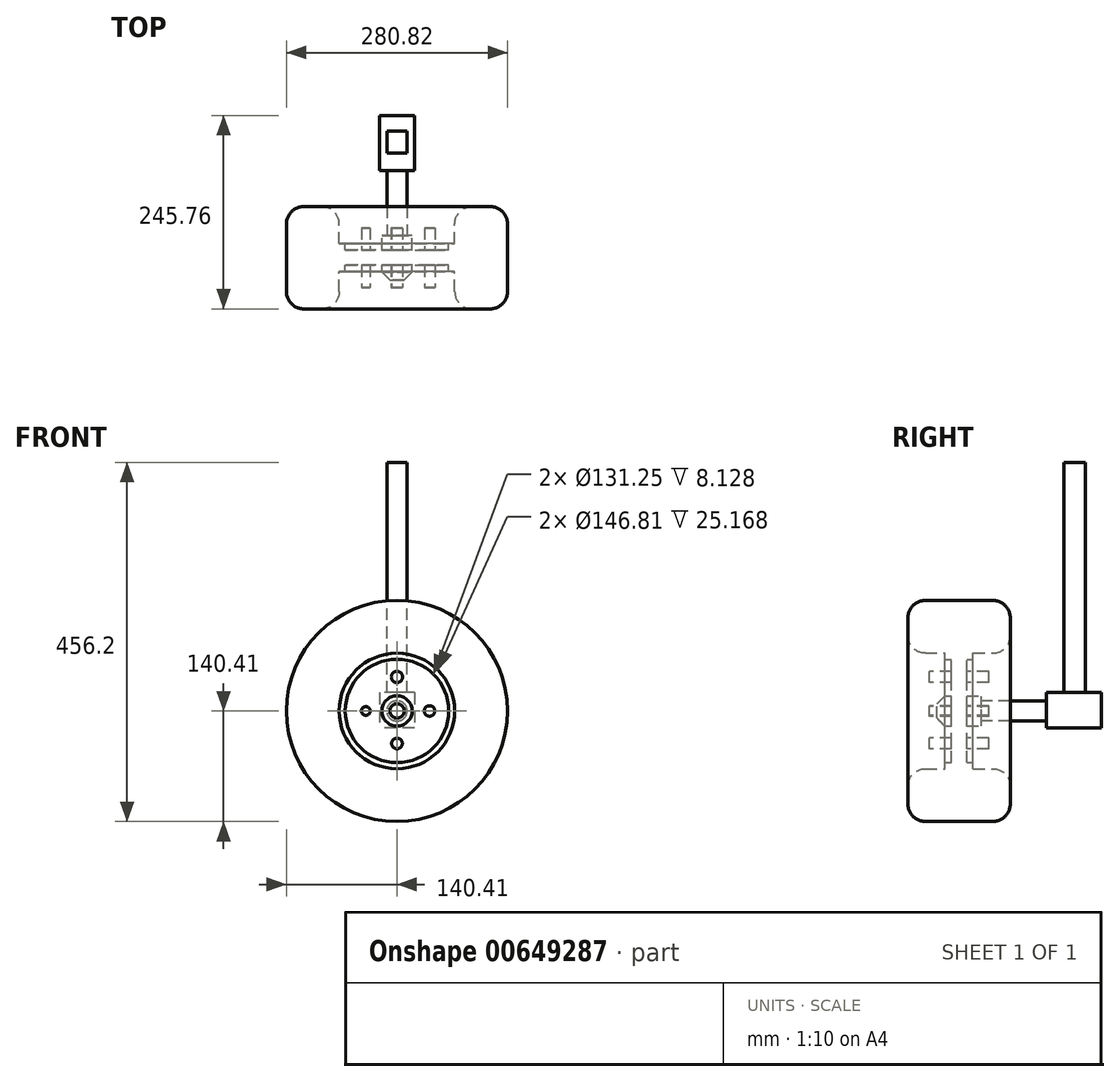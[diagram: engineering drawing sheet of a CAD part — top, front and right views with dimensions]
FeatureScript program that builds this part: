
annotation { "Feature Type Name" : "Feature", "Feature Type Description" : "" }
export const myFeature = defineFeature(function(context is Context, id is Id, definition is map)
    precondition{}
    {
        {
            var Q0;
            Q0=qCreatedBy(makeId("Front.planeOp"),FACE);
            var sketch = newSketch(context, id + "F0", { "sketchPlane" : qUnion([Q0])});
            skCircle(sketch, "E0", {"center": v(0, 0) * mm, "radius": 19.27 * mm});
            skSolve(sketch);
        }
        {
            var Q0;
            Q0 = qSketchRegion(id + "F0", true);
            extrude(context, id + "F1", {"entities" : qUnion([Q0]), "endBound" : BoundingType.SYMMETRIC, "depth" : 56.4 * mm, "offsetDistance" : 25.4 * mm});
        }
        {
            var Q0;
            Q0=qCreatedBy(makeId("Front.planeOp"),FACE);
            var sketch = newSketch(context, id + "F2", { "sketchPlane" : qUnion([Q0])});
            skCircle(sketch, "E1", {"center": v(0, 0) * mm, "radius": 76.72 * mm});
            skSolve(sketch);
        }
        {
            var Q0;
            Q0 = qSketchRegion(id + "F2", true);
            extrude(context, id + "F3", {"entities" : qUnion([Q0]), "operationType" : NewBodyOperationType.ADD, "endBound" : BoundingType.SYMMETRIC, "oppositeDirection" : true, "depth" : 19.3 * mm, "offsetDistance" : 25.4 * mm});
        }
        {
            var Q0;
            Q0=makeQuery(id+"F1.opExtrude","CAP_EDGE",EDGE,{"disambiguationData":[OSD([sQuery(id+"F0.wireOp",EDGE,"E0")])],"isStart":false});
            chamfer(context, id + "F4", {"entities" : qUnion([Q0]), "width" : 10.16 * mm, "tangentPropagation" : true});
        }
        {
            var Q0;
            Q0=qCreatedBy(makeId("Front.planeOp"),FACE);
            var sketch = newSketch(context, id + "F5", { "sketchPlane" : qUnion([Q0])});
            skCircle(sketch, "E2", {"center": v(0, 0) * mm, "radius": 65.62 * mm});
            skCircle(sketch, "E3", {"center": v(0, 0) * mm, "radius": 76.62 * mm});
            skSolve(sketch);
        }
        {
            var Q0;
            Q0 = qSketchRegion(id + "F5", true);
            extrude(context, id + "F6", {"entities" : qUnion([Q0]), "operationType" : NewBodyOperationType.ADD, "endBound" : BoundingType.SYMMETRIC, "depth" : 35.56 * mm, "offsetDistance" : 25.4 * mm});
        }
        {
            var Q0;
            Q0=qCreatedBy(makeId("Front.planeOp"),FACE);
            var sketch = newSketch(context, id + "F7", { "sketchPlane" : qUnion([Q0])});
            skCircle(sketch, "E4", {"center": v(0, 0) * mm, "radius": 140.41 * mm});
            skCircle(sketch, "E5", {"center": v(0, 0) * mm, "radius": 73.4 * mm});
            skSolve(sketch);
        }
        {
            var Q0;
            Q0 = qSketchRegion(id + "F7", true);
            extrude(context, id + "F8", {"entities" : qUnion([Q0]), "operationType" : NewBodyOperationType.ADD, "endBound" : BoundingType.SYMMETRIC, "depth" : 130.05 * mm, "offsetDistance" : 25.4 * mm});
        }
        {
            var Q0;
            Q0=makeQuery(id+"F8.opExtrude","CAP_EDGE",EDGE,{"disambiguationData":[OSD([sQuery(id+"F7.wireOp",EDGE,"E4")])],"isStart":true});
            var Q1;
            Q1=makeQuery(id+"F8.opExtrude","CAP_EDGE",EDGE,{"disambiguationData":[OSD([sQuery(id+"F7.wireOp",EDGE,"E5")])],"isStart":true});
            var Q2;
            Q2=makeQuery(id+"F8.opExtrude","CAP_EDGE",EDGE,{"disambiguationData":[OSD([sQuery(id+"F7.wireOp",EDGE,"E4")])],"isStart":false});
            var Q3;
            Q3=makeQuery(id+"F8.opExtrude","CAP_EDGE",EDGE,{"disambiguationData":[OSD([sQuery(id+"F7.wireOp",EDGE,"E5")])],"isStart":false});
            fillet(context, id + "F9", {"entities" : qUnion([Q0, Q1, Q2, Q3]), "radius" : 22.08 * mm, "tangentPropagation" : true, "allowEdgeOverflow" : false});
        }
        {
            var Q0;
            Q0=qCreatedBy(makeId("Front.planeOp"),FACE);
            var sketch = newSketch(context, id + "F10", { "sketchPlane" : qUnion([Q0])});
            skCircle(sketch, "E6", {"center": v(0, 43.2) * mm, "radius": 7.25 * mm});
            skCircle(sketch, "E7", {"center": v(41.43, 0) * mm, "radius": 6.66 * mm});
            skCircle(sketch, "E8", {"center": v(0, -41.27) * mm, "radius": 6.8 * mm});
            skCircle(sketch, "E9", {"center": v(-39.5, 0) * mm, "radius": 5.52 * mm});
            skSolve(sketch);
        }
        {
            var Q0;
            Q0 = qSketchRegion(id + "F10", true);
            extrude(context, id + "F11", {"entities" : qUnion([Q0]), "operationType" : NewBodyOperationType.ADD, "endBound" : BoundingType.SYMMETRIC, "oppositeDirection" : true, "depth" : 75.7 * mm, "offsetDistance" : 25.4 * mm});
        }
        {
            var Q0;
            Q0=qCreatedBy(makeId("Front.planeOp"),FACE);
            var sketch = newSketch(context, id + "F12", { "sketchPlane" : qUnion([Q0])});
            skCircle(sketch, "E10", {"center": v(0, 0) * mm, "radius": 12.9 * mm});
            skSolve(sketch);
        }
        {
            var Q0;
            Q0 = qSketchRegion(id + "F12", true);
            extrude(context, id + "F13", {"entities" : qUnion([Q0]), "operationType" : NewBodyOperationType.ADD, "oppositeDirection" : true, "depth" : 170.43 * mm, "offsetDistance" : 25.4 * mm});
        }
        {
            var Q0;
            Q0=qCreatedBy(makeId("Right.planeOp"),FACE);
            var sketch = newSketch(context, id + "F14", { "sketchPlane" : qUnion([Q0])});
            skLineSegment(sketch, "E11.bottom", {"start": v(180.74, 23.29) * mm, "end": v(110.71, 23.29) * mm});
            skLineSegment(sketch, "E11.top", {"start": v(180.74, -21.68) * mm, "end": v(110.71, -21.68) * mm});
            skLineSegment(sketch, "E11.left", {"start": v(180.74, 23.29) * mm, "end": v(180.74, -21.68) * mm});
            skLineSegment(sketch, "E11.right", {"start": v(110.71, 23.29) * mm, "end": v(110.71, -21.68) * mm});
            skSolve(sketch);
        }
        {
            var Q0;
            Q0 = qSketchRegion(id + "F14", true);
            extrude(context, id + "F15", {"entities" : qUnion([Q0]), "operationType" : NewBodyOperationType.ADD, "endBound" : BoundingType.SYMMETRIC, "depth" : 44.7 * mm, "offsetDistance" : 25.4 * mm});
        }
        {
            var Q0;
            Q0=qCreatedBy(makeId("Right.planeOp"),FACE);
            var sketch = newSketch(context, id + "F16", { "sketchPlane" : qUnion([Q0])});
            skLineSegment(sketch, "E12.bottom", {"start": v(160.58, 10.98) * mm, "end": v(133.08, 10.98) * mm});
            skLineSegment(sketch, "E12.top", {"start": v(160.58, 315.8) * mm, "end": v(133.08, 315.8) * mm});
            skLineSegment(sketch, "E12.left", {"start": v(160.58, 10.98) * mm, "end": v(160.58, 315.8) * mm});
            skLineSegment(sketch, "E12.right", {"start": v(133.08, 10.98) * mm, "end": v(133.08, 315.8) * mm});
            skSolve(sketch);
        }
        {
            var Q0;
            Q0 = qSketchRegion(id + "F16", true);
            extrude(context, id + "F17", {"entities" : qUnion([Q0]), "operationType" : NewBodyOperationType.ADD, "endBound" : BoundingType.SYMMETRIC, "depth" : 25.4 * mm, "offsetDistance" : 25.4 * mm});
        }
    });
